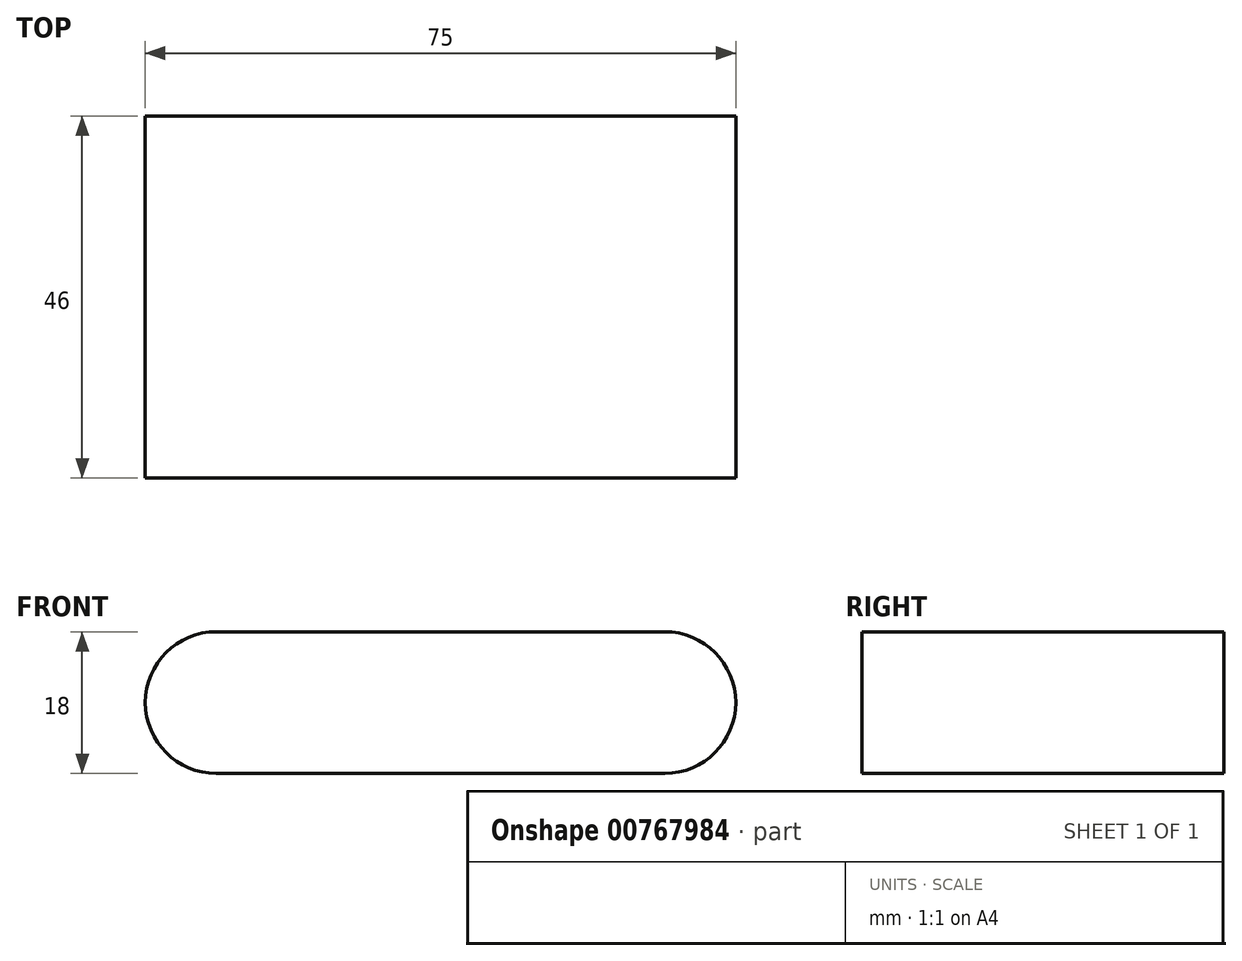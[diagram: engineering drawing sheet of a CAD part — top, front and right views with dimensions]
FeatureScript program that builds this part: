
annotation { "Feature Type Name" : "Feature", "Feature Type Description" : "" }
export const myFeature = defineFeature(function(context is Context, id is Id, definition is map)
    precondition{}
    {
        {
            var Q0;
            Q0=qCreatedBy(makeId("Top.planeOp"),FACE);
            var sketch = newSketch(context, id + "F0", { "sketchPlane" : qUnion([Q0])});
            skLineSegment(sketch, "E0.bottom", {"start": v(37.5, 23) * mm, "end": v(-37.5, 23) * mm});
            skLineSegment(sketch, "E0.top", {"start": v(37.5, -23) * mm, "end": v(-37.5, -23) * mm});
            skLineSegment(sketch, "E0.left", {"start": v(37.5, 23) * mm, "end": v(37.5, -23) * mm});
            skLineSegment(sketch, "E0.right", {"start": v(-37.5, 23) * mm, "end": v(-37.5, -23) * mm});
            skPoint(sketch, "E0.middle", {"position": v(0, 0) * mm});
            skSolve(sketch);
        }
        {
            var Q0;
            Q0 = qSketchRegion(id + "F0", true);
            extrude(context, id + "F1", {"entities" : qUnion([Q0]), "depth" : 18 * mm, "offsetDistance" : 25 * mm});
        }
        {
            var Q0;
            Q0=makeQuery(id+"F1.opExtrude","CAP_EDGE",EDGE,{"disambiguationData":[OSD([sQuery(id+"F0.wireOp",EDGE,"E0.left")])],"isStart":false});
            var Q1;
            Q1=makeQuery(id+"F1.opExtrude","CAP_EDGE",EDGE,{"disambiguationData":[OSD([sQuery(id+"F0.wireOp",EDGE,"E0.left")])],"isStart":true});
            var Q2;
            Q2=makeQuery(id+"F1.opExtrude","CAP_EDGE",EDGE,{"disambiguationData":[OSD([sQuery(id+"F0.wireOp",EDGE,"E0.right")])],"isStart":true});
            var Q3;
            Q3=makeQuery(id+"F1.opExtrude","CAP_EDGE",EDGE,{"disambiguationData":[OSD([sQuery(id+"F0.wireOp",EDGE,"E0.right")])],"isStart":false});
            fillet(context, id + "F2", {"entities" : qUnion([Q0, Q1, Q2, Q3]), "radius" : 9 * mm, "tangentPropagation" : true, "allowEdgeOverflow" : false});
        }
    });
